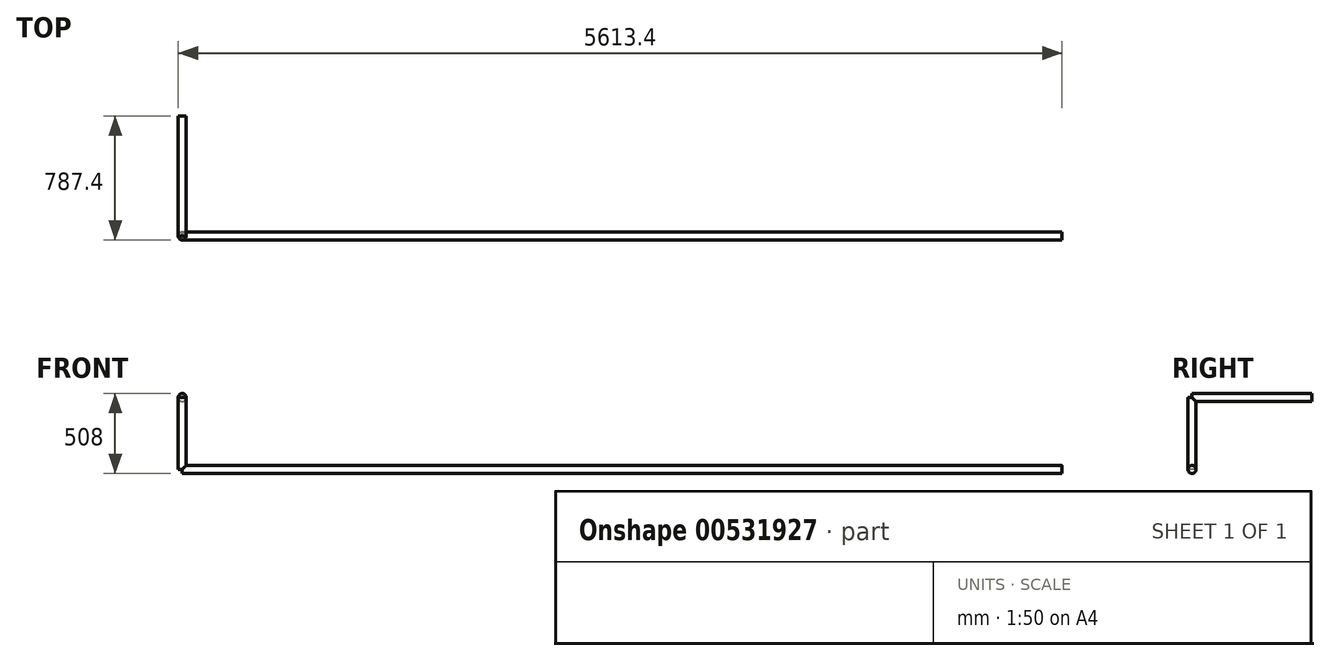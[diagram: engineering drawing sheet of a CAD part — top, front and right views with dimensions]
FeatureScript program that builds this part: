
annotation { "Feature Type Name" : "Feature", "Feature Type Description" : "" }
export const myFeature = defineFeature(function(context is Context, id is Id, definition is map)
    precondition{}
    {
        {
            var Q0;
            Q0=qCreatedBy(makeId("Right.planeOp"),FACE);
            var sketch = newSketch(context, id + "F0", { "sketchPlane" : qUnion([Q0])});
            skCircle(sketch, "E0", {"center": v(0, 0) * mm, "radius": 25.4 * mm});
            skSolve(sketch);
        }
        {
            var Q0;
            Q0 = qSketchRegion(id + "F0", true);
            extrude(context, id + "F1", {"entities" : qUnion([Q0]), "depth" : 5588 * mm, "offsetDistance" : 25.4 * mm});
        }
        {
            var Q0;
            Q0=qCreatedBy(makeId("Top.planeOp"),FACE);
            var sketch = newSketch(context, id + "F2", { "sketchPlane" : qUnion([Q0])});
            skCircle(sketch, "E1", {"center": v(0, 0) * mm, "radius": 25.4 * mm});
            skSolve(sketch);
        }
        {
            var Q0;
            Q0 = qSketchRegion(id + "F2", true);
            extrude(context, id + "F3", {"entities" : qUnion([Q0]), "operationType" : NewBodyOperationType.ADD, "depth" : 457.2 * mm, "offsetDistance" : 25.4 * mm});
        }
        {
            var Q0;
            Q0=makeQuery(id+"F3.opExtrude","CAP_FACE",FACE,{"disambiguationData":[OSD([sQuery(id+"F2.wireOp",EDGE,"E1")])],"isStart":false});
            var sketch = newSketch(context, id + "F4", { "sketchPlane" : qUnion([Q0])});
            skPoint(sketch, "E2", {"position": v(0, 0) * mm});
            skSolve(sketch);
        }
        {
            var Q0;
            Q0=qCreatedBy(makeId("Front.planeOp"),FACE);
            var sketch = newSketch(context, id + "F5", { "sketchPlane" : qUnion([Q0])});
            skCircle(sketch, "E3", {"center": v(0, 457.2) * mm, "radius": 25.4 * mm});
            skSolve(sketch);
        }
        {
            var Q0;
            Q0 = qSketchRegion(id + "F5", true);
            extrude(context, id + "F6", {"entities" : qUnion([Q0]), "operationType" : NewBodyOperationType.ADD, "oppositeDirection" : true, "depth" : 762 * mm, "offsetDistance" : 25.4 * mm});
        }
    });
